# Revit family: QF_COMENDA_6F0081_6F0081DR_CAT
name_source: partatom
category: Attrezzature speciali
units: mm (PartAtom-declared; Revit-internal decimal feet)

## family parameters
Basato su piano di lavoro = No
Condiviso = No
Numero OmniClass = 23.40.40.14
Punto di calcolo locali = No
Quota connettore circolare = Usa diametro
Sempre verticale = Sì
Taglio con vuoti quando caricato = No
Tipo di parte = Normale
Titolo OmniClass = Food Service Equipment

## types (2) — shared parameters
Altezza = 820 mm  [stored 2.69029 ft]
Altezza allacciamento elettrico da pavimento finito = 83 mm  [stored 0.27231 ft]
Altezza da terra raccordo acqua calda = 64 mm  [stored 0.209974 ft]
Altezza dello scarico diretto acqua da pavimento finito = 64 mm  [stored 0.209974 ft]
Base stand with door = No
Corrente di funzionamento normale = 23 A
Diametro dello scarico diretto di acqua = 1 1/2"
Diametro raccordo acqua calda = 1"
Fase = 3
Frequenza = 50 Hz
Lunghezza = 600 mm
Numero dei poli = 3
Peso netto = 71.00 kg
Potenza elettrica = 9650 W
Pressione minima acqua calda = 2000.0 Pa
Produttore = COMENDA
Profondità = 600 mm
Protezione contro le sovracorrenti = 25 A
Stand feet kit = No
Temperatura raccomandata per acqua calda = 50 °C
Tensione = 400 V
URL = www.comenda.eu
URL catalogo = https://comenda.eu
zero-valued in all types: HEIGHT FROM THE FLOOR, Prospetto di default

## per-type parameters (varying)
| type | Descrizione | Modello |
| 6F0081 | DUAL WALL MULTIPOWER DISHWASHER WITH HR DRAIN PUMP, PERISTALTIC DOSING UNITS AND RCD | TF45 R |
| 6F0081DR | DUAL WALL MULTIPOWER DOUBLE RACK DISHWASHER WITH HR DRAIN PUMP, PERISTALTIC DOSING UNITS AND RCD | TF45 R DR |

note: [stored X ft] marks values corroborated as IEEE doubles in the binary element streams (Revit-internal decimal feet)

## geometry (parser evidence)
native form markers: Sweep x1
no freeform markers — native parametric forms only
